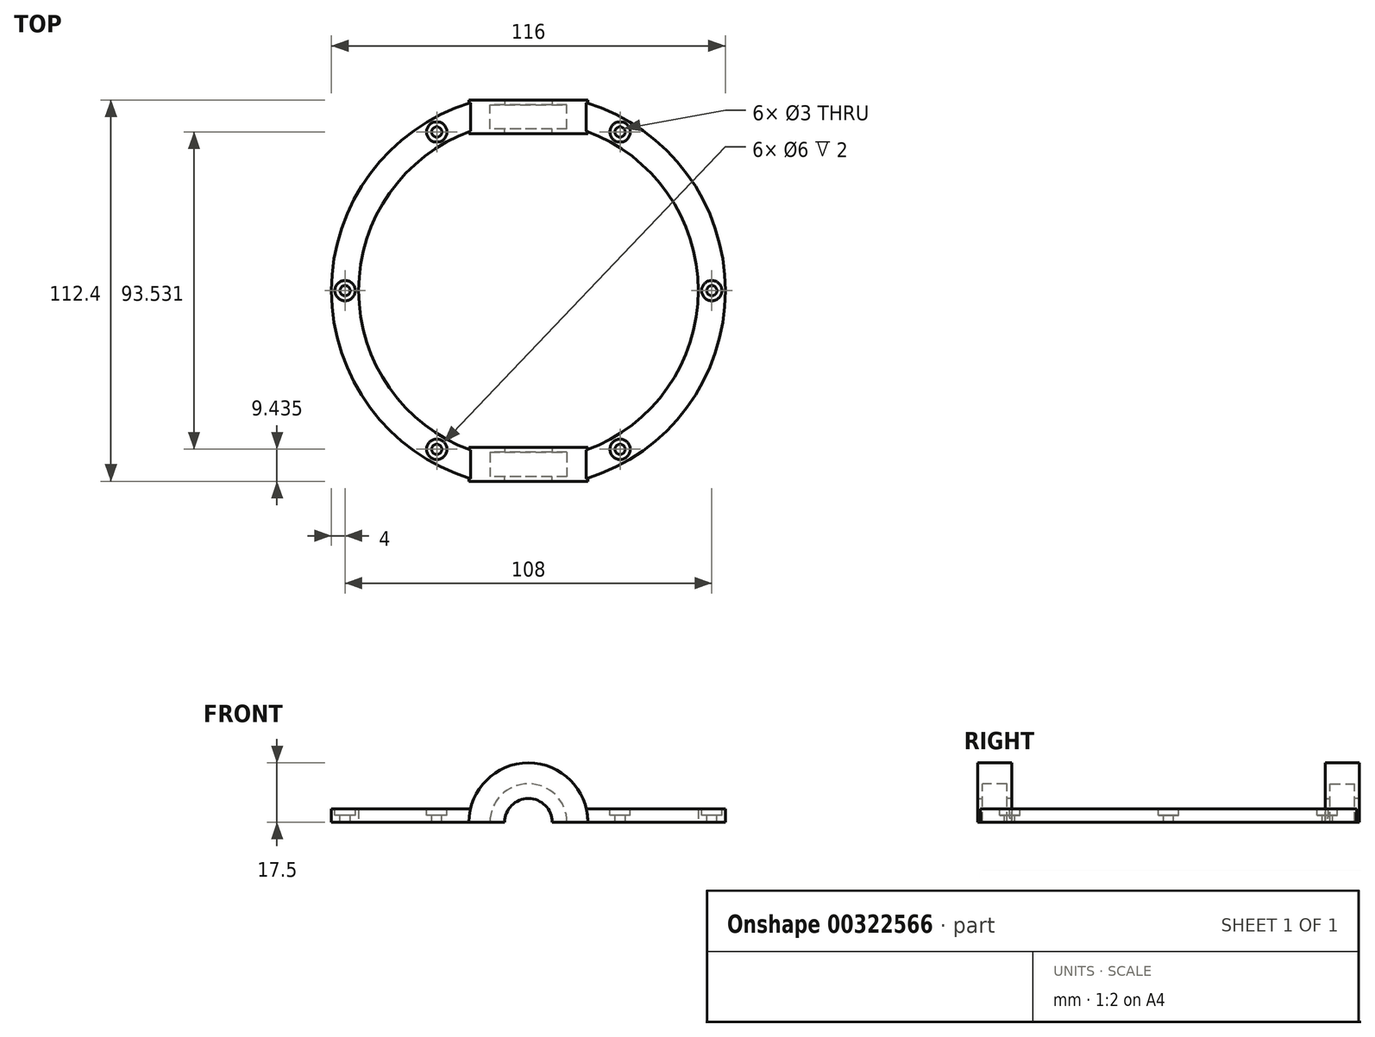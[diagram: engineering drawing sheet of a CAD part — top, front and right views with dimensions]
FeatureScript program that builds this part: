
annotation { "Feature Type Name" : "Feature", "Feature Type Description" : "" }
export const myFeature = defineFeature(function(context is Context, id is Id, definition is map)
    precondition{}
    {
        {
            var Q0;
            Q0=qCreatedBy(makeId("Top.planeOp"),FACE);
            var sketch = newSketch(context, id + "F0", { "sketchPlane" : qUnion([Q0])});
            skCircle(sketch, "E0", {"center": v(0, 0) * mm, "radius": 50 * mm});
            skCircle(sketch, "E1", {"center": v(0, 0) * mm, "radius": 58 * mm});
            skSolve(sketch);
        }
        {
            var Q0;
            Q0 = qSketchRegion(id + "F0", true);
            extrude(context, id + "F1", {"entities" : qUnion([Q0]), "depth" : 4 * mm, "hasSecondDirection" : true, "secondDirectionOppositeDirection" : true, "secondDirectionDepth" : 4 * mm});
        }
        {
            var Q0;
            Q0=qCreatedBy(makeId("Front.planeOp"),FACE);
            cPlane(context, id + "F2", {"entities" : qUnion([Q0]), "cplaneType" : CPlaneType.OFFSET, "offset" : 54.8 * mm, "width" : 150 * mm, "height" : 150 * mm});
        }
        {
            var Q0;
            Q0=qCreatedBy(id+"F2.planeOp",FACE);
            var sketch = newSketch(context, id + "F3", { "sketchPlane" : qUnion([Q0])});
            skCircle(sketch, "E2", {"center": v(0, 0) * mm, "radius": 11.35 * mm});
            skCircle(sketch, "E3", {"center": v(0, 0) * mm, "radius": 17.5 * mm});
            skSolve(sketch);
        }
        {
            var Q0;
            Q0=makeQuery(id+"F3.imprint","IMPRINT",FACE,{"disambiguationData":[TD([[makeQuery(id+"F3.imprint","IMPRINT",EDGE,{"derivedFrom":sQuery(id+"F3.wireOp",EDGE,"E2")}),1.0]])]});
            var Q1;
            Q1=makeQuery(id+"F3.imprint","IMPRINT",FACE,{"disambiguationData":[TD([[makeQuery(id+"F3.imprint","IMPRINT",EDGE,{"derivedFrom":sQuery(id+"F3.wireOp",EDGE,"E2")}),-1.0]])]});
            extrude(context, id + "F4", {"entities" : qUnion([Q0, Q1]), "operationType" : NewBodyOperationType.REMOVE, "oppositeDirection" : true, "depth" : 25 * mm, "hasSecondDirection" : true, "secondDirectionOppositeDirection" : false, "secondDirectionDepth" : 25 * mm});
        }
        {
            var Q0;
            Q0=makeQuery(id+"F3.imprint","IMPRINT",FACE,{"disambiguationData":[TD([[makeQuery(id+"F3.imprint","IMPRINT",EDGE,{"derivedFrom":sQuery(id+"F3.wireOp",EDGE,"E2")}),-1.0]])]});
            extrude(context, id + "F5", {"entities" : qUnion([Q0]), "operationType" : NewBodyOperationType.ADD, "oppositeDirection" : true, "depth" : 7.2 * mm});
        }
        {
            var Q0;
            Q0=makeQuery(id+"F5.opExtrude","CAP_FACE",FACE,{"disambiguationData":[OSD([sQuery(id+"F3.wireOp",EDGE,"E2"),sQuery(id+"F3.wireOp",EDGE,"E3")])],"isStart":true});
            var sketch = newSketch(context, id + "F6", { "sketchPlane" : qUnion([Q0])});
            skCircle(sketch, "E4", {"center": v(0, 0) * mm, "radius": 7 * mm});
            skCircle(sketch, "E5", {"center": v(0, 0) * mm, "radius": 17.5 * mm});
            skSolve(sketch);
        }
        {
            var Q0;
            Q0=makeQuery(id+"F6.imprint","IMPRINT",FACE,{"disambiguationData":[TD([[makeQuery(id+"F6.imprint","IMPRINT",EDGE,{"derivedFrom":sQuery(id+"F6.wireOp",EDGE,"E4")}),-1.0]])]});
            var Q1;
            Q1=makeQuery(id+"F6.imprint","IMPRINT",FACE,{"disambiguationData":[TD([[makeQuery(id+"F6.imprint","IMPRINT",EDGE,{"derivedFrom":sQuery(id+"F6.wireOp",EDGE,"E5")}),1.0]])]});
            extrude(context, id + "F7", {"entities" : qUnion([Q0, Q1]), "operationType" : NewBodyOperationType.ADD, "depth" : 1.4 * mm});
        }
        {
            var Q0;
            Q0=makeQuery(id+"F5.opExtrude","CAP_FACE",FACE,{"disambiguationData":[OSD([sQuery(id+"F3.wireOp",EDGE,"E2"),sQuery(id+"F3.wireOp",EDGE,"E3")])],"isStart":false});
            var sketch = newSketch(context, id + "F8", { "sketchPlane" : qUnion([Q0])});
            skCircle(sketch, "E6", {"center": v(0, 0) * mm, "radius": 7 * mm});
            skCircle(sketch, "E7", {"center": v(0, 0) * mm, "radius": 17.5 * mm});
            skSolve(sketch);
        }
        {
            var Q0;
            Q0=makeQuery(id+"F8.imprint","IMPRINT",FACE,{"disambiguationData":[TD([[makeQuery(id+"F8.imprint","IMPRINT",EDGE,{"derivedFrom":sQuery(id+"F8.wireOp",EDGE,"E7")}),-1.0]])]});
            var Q1;
            Q1=makeQuery(id+"F8.imprint","IMPRINT",FACE,{"disambiguationData":[TD([[makeQuery(id+"F8.imprint","IMPRINT",EDGE,{"derivedFrom":sQuery(id+"F8.wireOp",EDGE,"E6")}),-1.0]])]});
            extrude(context, id + "F9", {"entities" : qUnion([Q0, Q1]), "operationType" : NewBodyOperationType.ADD, "depth" : 1.4 * mm});
        }
        {
            var Q0;
            Q0=qCreatedBy(makeId("Front.planeOp"),FACE);
            cPlane(context, id + "F10", {"entities" : qUnion([Q0]), "cplaneType" : CPlaneType.OFFSET, "offset" : 54.8 * mm, "oppositeDirection" : true, "width" : 150 * mm, "height" : 150 * mm});
        }
        {
            var Q0;
            Q0=qCreatedBy(id+"F10.planeOp",FACE);
            var sketch = newSketch(context, id + "F11", { "sketchPlane" : qUnion([Q0])});
            skCircle(sketch, "E8", {"center": v(0, 0) * mm, "radius": 17.5 * mm});
            skCircle(sketch, "E9", {"center": v(0, 0) * mm, "radius": 11.35 * mm});
            skSolve(sketch);
        }
        {
            var Q0;
            Q0=makeQuery(id+"F11.imprint","IMPRINT",FACE,{"disambiguationData":[TD([[makeQuery(id+"F11.imprint","IMPRINT",EDGE,{"derivedFrom":sQuery(id+"F11.wireOp",EDGE,"E8")}),1.0]])]});
            var Q1;
            Q1=makeQuery(id+"F11.imprint","IMPRINT",FACE,{"disambiguationData":[TD([[makeQuery(id+"F11.imprint","IMPRINT",EDGE,{"derivedFrom":sQuery(id+"F11.wireOp",EDGE,"E9")}),1.0]])]});
            extrude(context, id + "F12", {"entities" : qUnion([Q0, Q1]), "operationType" : NewBodyOperationType.REMOVE, "depth" : 25 * mm, "hasSecondDirection" : true, "secondDirectionOppositeDirection" : true, "secondDirectionDepth" : 25 * mm});
        }
        {
            var Q0;
            Q0=makeQuery(id+"F11.imprint","IMPRINT",FACE,{"disambiguationData":[TD([[makeQuery(id+"F11.imprint","IMPRINT",EDGE,{"derivedFrom":sQuery(id+"F11.wireOp",EDGE,"E8")}),1.0]])]});
            extrude(context, id + "F13", {"entities" : qUnion([Q0]), "operationType" : NewBodyOperationType.ADD, "depth" : 7.2 * mm});
        }
        {
            var Q0;
            Q0=makeQuery(id+"F13.opExtrude","CAP_FACE",FACE,{"disambiguationData":[OSD([sQuery(id+"F11.wireOp",EDGE,"E8"),sQuery(id+"F11.wireOp",EDGE,"E9")])],"isStart":true});
            var sketch = newSketch(context, id + "F14", { "sketchPlane" : qUnion([Q0])});
            skCircle(sketch, "E10", {"center": v(0, 0) * mm, "radius": 7 * mm});
            skCircle(sketch, "E11", {"center": v(0, 0) * mm, "radius": 17.5 * mm});
            skSolve(sketch);
        }
        {
            var Q0;
            Q0=makeQuery(id+"F14.imprint","IMPRINT",FACE,{"disambiguationData":[TD([[makeQuery(id+"F14.imprint","IMPRINT",EDGE,{"derivedFrom":makeQuery(id+"F13.opExtrude","CAP_EDGE",EDGE,{"disambiguationData":[OSD([sQuery(id+"F11.wireOp",EDGE,"E9")])],"isStart":true})}),1.0]])]});
            var Q1;
            Q1=makeQuery(id+"F14.imprint","IMPRINT",FACE,{"disambiguationData":[TD([[makeQuery(id+"F14.imprint","IMPRINT",EDGE,{"derivedFrom":sQuery(id+"F14.wireOp",EDGE,"E10")}),-1.0]])]});
            extrude(context, id + "F15", {"entities" : qUnion([Q0, Q1]), "operationType" : NewBodyOperationType.ADD, "depth" : 1.4 * mm});
        }
        {
            var Q0;
            Q0=makeQuery(id+"F13.opExtrude","CAP_FACE",FACE,{"disambiguationData":[OSD([sQuery(id+"F11.wireOp",EDGE,"E8"),sQuery(id+"F11.wireOp",EDGE,"E9")])],"isStart":false});
            var sketch = newSketch(context, id + "F16", { "sketchPlane" : qUnion([Q0])});
            skCircle(sketch, "E12", {"center": v(0, 0) * mm, "radius": 7 * mm});
            skCircle(sketch, "E13", {"center": v(0, 0) * mm, "radius": 17.5 * mm});
            skSolve(sketch);
        }
        {
            var Q0;
            Q0=makeQuery(id+"F16.imprint","IMPRINT",FACE,{"disambiguationData":[TD([[makeQuery(id+"F16.imprint","IMPRINT",EDGE,{"derivedFrom":sQuery(id+"F16.wireOp",EDGE,"E12")}),-1.0]])]});
            var Q1;
            Q1=makeQuery(id+"F16.imprint","IMPRINT",FACE,{"disambiguationData":[TD([[makeQuery(id+"F16.imprint","IMPRINT",EDGE,{"derivedFrom":sQuery(id+"F16.wireOp",EDGE,"E13")}),1.0]])]});
            extrude(context, id + "F17", {"entities" : qUnion([Q0, Q1]), "operationType" : NewBodyOperationType.ADD, "depth" : 1.4 * mm});
        }
        {
            var Q0;
            Q0=makeQuery(id+"F12.boolean.opBoolean","SPLIT",FACE,{"disambiguationData":[OD(0.0)],"derivedFrom":makeQuery(id+"F1.opExtrude","CAP_FACE",FACE,{"disambiguationData":[OSD([sQuery(id+"F0.wireOp",EDGE,"E0"),sQuery(id+"F0.wireOp",EDGE,"E1")])],"isStart":false})});
            var sketch = newSketch(context, id + "F18", { "sketchPlane" : qUnion([Q0])});
            skLineSegment(sketch, "E14", {"start": v(0, 0) * mm, "end": v(-50, 0) * mm, "construction": true});
            skLineSegment(sketch, "E15", {"start": v(-50, 0) * mm, "end": v(-58, 0) * mm, "construction": true});
            skCircle(sketch, "E16", {"center": v(-54, 0) * mm, "radius": 3 * mm});
            skCircle(sketch, "E17", {"center": v(-54, 0) * mm, "radius": 1.5 * mm});
            skCircle(sketch, "E18", {"center": v(-54, 0) * mm, "radius": 1 * mm});
            skCircle(sketch, "E19.1.0", {"center": v(-27, -46.77) * mm, "radius": 3 * mm});
            skCircle(sketch, "E19.1.1", {"center": v(-27, -46.77) * mm, "radius": 1.5 * mm});
            skCircle(sketch, "E19.1.2", {"center": v(-27, -46.77) * mm, "radius": 1 * mm});
            skCircle(sketch, "E19.2.0", {"center": v(27, -46.77) * mm, "radius": 3 * mm});
            skCircle(sketch, "E19.2.1", {"center": v(27, -46.77) * mm, "radius": 1.5 * mm});
            skCircle(sketch, "E19.2.2", {"center": v(27, -46.77) * mm, "radius": 1 * mm});
            skCircle(sketch, "E19.3.0", {"center": v(54, 0) * mm, "radius": 3 * mm});
            skCircle(sketch, "E19.3.1", {"center": v(54, 0) * mm, "radius": 1.5 * mm});
            skCircle(sketch, "E19.3.2", {"center": v(54, 0) * mm, "radius": 1 * mm});
            skCircle(sketch, "E19.4.0", {"center": v(27, 46.77) * mm, "radius": 3 * mm});
            skCircle(sketch, "E19.4.1", {"center": v(27, 46.77) * mm, "radius": 1.5 * mm});
            skCircle(sketch, "E19.4.2", {"center": v(27, 46.77) * mm, "radius": 1 * mm});
            skCircle(sketch, "E19.5.0", {"center": v(-27, 46.77) * mm, "radius": 3 * mm});
            skCircle(sketch, "E19.5.1", {"center": v(-27, 46.77) * mm, "radius": 1.5 * mm});
            skCircle(sketch, "E19.5.2", {"center": v(-27, 46.77) * mm, "radius": 1 * mm});
            skPoint(sketch, "E19.center", {"position": v(0, 0) * mm});
            skSolve(sketch);
        }
        {
            var Q0;
            Q0=makeQuery(id+"F18.imprint","IMPRINT",FACE,{"disambiguationData":[TD([[makeQuery(id+"F18.imprint","IMPRINT",EDGE,{"derivedFrom":sQuery(id+"F18.wireOp",EDGE,"E18")}),1.0]])]});
            var Q1;
            Q1=makeQuery(id+"F18.imprint","IMPRINT",FACE,{"disambiguationData":[TD([[makeQuery(id+"F18.imprint","IMPRINT",EDGE,{"derivedFrom":sQuery(id+"F18.wireOp",EDGE,"E19.5.2")}),1.0]])]});
            var Q2;
            Q2=makeQuery(id+"F18.imprint","IMPRINT",FACE,{"disambiguationData":[TD([[makeQuery(id+"F18.imprint","IMPRINT",EDGE,{"derivedFrom":sQuery(id+"F18.wireOp",EDGE,"E19.4.2")}),1.0]])]});
            var Q3;
            Q3=makeQuery(id+"F18.imprint","IMPRINT",FACE,{"disambiguationData":[TD([[makeQuery(id+"F18.imprint","IMPRINT",EDGE,{"derivedFrom":sQuery(id+"F18.wireOp",EDGE,"E19.3.2")}),1.0]])]});
            var Q4;
            Q4=makeQuery(id+"F18.imprint","IMPRINT",FACE,{"disambiguationData":[TD([[makeQuery(id+"F18.imprint","IMPRINT",EDGE,{"derivedFrom":sQuery(id+"F18.wireOp",EDGE,"E19.2.2")}),1.0]])]});
            var Q5;
            Q5=makeQuery(id+"F18.imprint","IMPRINT",FACE,{"disambiguationData":[TD([[makeQuery(id+"F18.imprint","IMPRINT",EDGE,{"derivedFrom":sQuery(id+"F18.wireOp",EDGE,"E19.1.2")}),1.0]])]});
            extrude(context, id + "F19", {"entities" : qUnion([Q0, Q1, Q2, Q3, Q4, Q5]), "operationType" : NewBodyOperationType.REMOVE, "oppositeDirection" : true, "depth" : 25 * mm});
        }
        {
            var Q0;
            Q0=makeQuery(id+"F18.imprint","IMPRINT",FACE,{"disambiguationData":[TD([[makeQuery(id+"F18.imprint","IMPRINT",EDGE,{"derivedFrom":sQuery(id+"F18.wireOp",EDGE,"E17")}),1.0]])]});
            var Q1;
            Q1=makeQuery(id+"F18.imprint","IMPRINT",FACE,{"disambiguationData":[TD([[makeQuery(id+"F18.imprint","IMPRINT",EDGE,{"derivedFrom":sQuery(id+"F18.wireOp",EDGE,"E19.5.1")}),1.0]])]});
            var Q2;
            Q2=makeQuery(id+"F18.imprint","IMPRINT",FACE,{"disambiguationData":[TD([[makeQuery(id+"F18.imprint","IMPRINT",EDGE,{"derivedFrom":sQuery(id+"F18.wireOp",EDGE,"E19.4.1")}),1.0]])]});
            var Q3;
            Q3=makeQuery(id+"F18.imprint","IMPRINT",FACE,{"disambiguationData":[TD([[makeQuery(id+"F18.imprint","IMPRINT",EDGE,{"derivedFrom":sQuery(id+"F18.wireOp",EDGE,"E19.3.1")}),1.0]])]});
            var Q4;
            Q4=makeQuery(id+"F18.imprint","IMPRINT",FACE,{"disambiguationData":[TD([[makeQuery(id+"F18.imprint","IMPRINT",EDGE,{"derivedFrom":sQuery(id+"F18.wireOp",EDGE,"E19.2.1")}),1.0]])]});
            var Q5;
            Q5=makeQuery(id+"F18.imprint","IMPRINT",FACE,{"disambiguationData":[TD([[makeQuery(id+"F18.imprint","IMPRINT",EDGE,{"derivedFrom":sQuery(id+"F18.wireOp",EDGE,"E19.1.1")}),1.0]])]});
            extrude(context, id + "F20", {"entities" : qUnion([Q0, Q1, Q2, Q3, Q4, Q5]), "operationType" : NewBodyOperationType.REMOVE, "oppositeDirection" : true, "depth" : 4 * mm});
        }
        {
            var Q0;
            Q0=makeQuery(id+"F18.imprint","IMPRINT",FACE,{"disambiguationData":[TD([[makeQuery(id+"F18.imprint","IMPRINT",EDGE,{"derivedFrom":sQuery(id+"F18.wireOp",EDGE,"E16")}),1.0]])]});
            var Q1;
            Q1=makeQuery(id+"F18.imprint","IMPRINT",FACE,{"disambiguationData":[TD([[makeQuery(id+"F18.imprint","IMPRINT",EDGE,{"derivedFrom":sQuery(id+"F18.wireOp",EDGE,"E19.1.0")}),1.0]])]});
            var Q2;
            Q2=makeQuery(id+"F18.imprint","IMPRINT",FACE,{"disambiguationData":[TD([[makeQuery(id+"F18.imprint","IMPRINT",EDGE,{"derivedFrom":sQuery(id+"F18.wireOp",EDGE,"E19.2.0")}),1.0]])]});
            var Q3;
            Q3=makeQuery(id+"F18.imprint","IMPRINT",FACE,{"disambiguationData":[TD([[makeQuery(id+"F18.imprint","IMPRINT",EDGE,{"derivedFrom":sQuery(id+"F18.wireOp",EDGE,"E19.3.0")}),1.0]])]});
            var Q4;
            Q4=makeQuery(id+"F18.imprint","IMPRINT",FACE,{"disambiguationData":[TD([[makeQuery(id+"F18.imprint","IMPRINT",EDGE,{"derivedFrom":sQuery(id+"F18.wireOp",EDGE,"E19.4.0")}),1.0]])]});
            var Q5;
            Q5=makeQuery(id+"F18.imprint","IMPRINT",FACE,{"disambiguationData":[TD([[makeQuery(id+"F18.imprint","IMPRINT",EDGE,{"derivedFrom":sQuery(id+"F18.wireOp",EDGE,"E19.5.0")}),1.0]])]});
            extrude(context, id + "F21", {"entities" : qUnion([Q0, Q1, Q2, Q3, Q4, Q5]), "operationType" : NewBodyOperationType.REMOVE, "oppositeDirection" : true, "depth" : 2 * mm});
        }
        {
            var Q0;
            Q0=qCreatedBy(makeId("Top.planeOp"),FACE);
            var sketch = newSketch(context, id + "F22", { "sketchPlane" : qUnion([Q0])});
            skCircle(sketch, "E20", {"center": v(0, 0) * mm, "radius": 72.87 * mm});
            skSolve(sketch);
        }
        {
            var Q0;
            Q0 = qSketchRegion(id + "F22", true);
            extrude(context, id + "F23", {"entities" : qUnion([Q0]), "operationType" : NewBodyOperationType.REMOVE, "oppositeDirection" : true, "depth" : 25 * mm});
        }
    });
